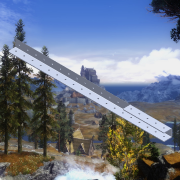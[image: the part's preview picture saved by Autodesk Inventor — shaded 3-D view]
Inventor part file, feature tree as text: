
AUTODESK INVENTOR PART (.ipt)
format: ipt  version: 2015 SP1 (Build 190203100, 203)  size: 426,496 bytes
history: native  units: in
note: dims shown in document units (in); Inventor stores cm internally (conversion verified against a paired STEP export)
features: other x2, extrude x2, sketch x2, plane x1, imported_body x1, projected_geometry x1
ambient origin geometry x8: Origin, YZ Plane, XZ Plane, XY Plane, X Axis, Y Axis, Z Axis, Center Point
bodies: Body1 (feature_tree)
feature tree (9):
  other  "Break-Corner1"
  other  "VersaFrame 1 x 1 x 1 x 0.090 C-Channel (59 length)(217-4107)1"
  plane  "Work Plane1"
  extrude  "Extrusion1"  Depth=1.0in TaperAngle=0.0deg
  extrude  "Extrusion3"  Depth=0.5in TaperAngle=0.0deg
  imported_body  "Base1"
  sketch  "Sketch1"  dims[d0=19.0in d1=1.0in d2=0.0in]
  sketch  "Sketch2"  dims[d5=5.0in d6=0.5in d7=0.0in]
  projected_geometry  "Projected Loop1"
